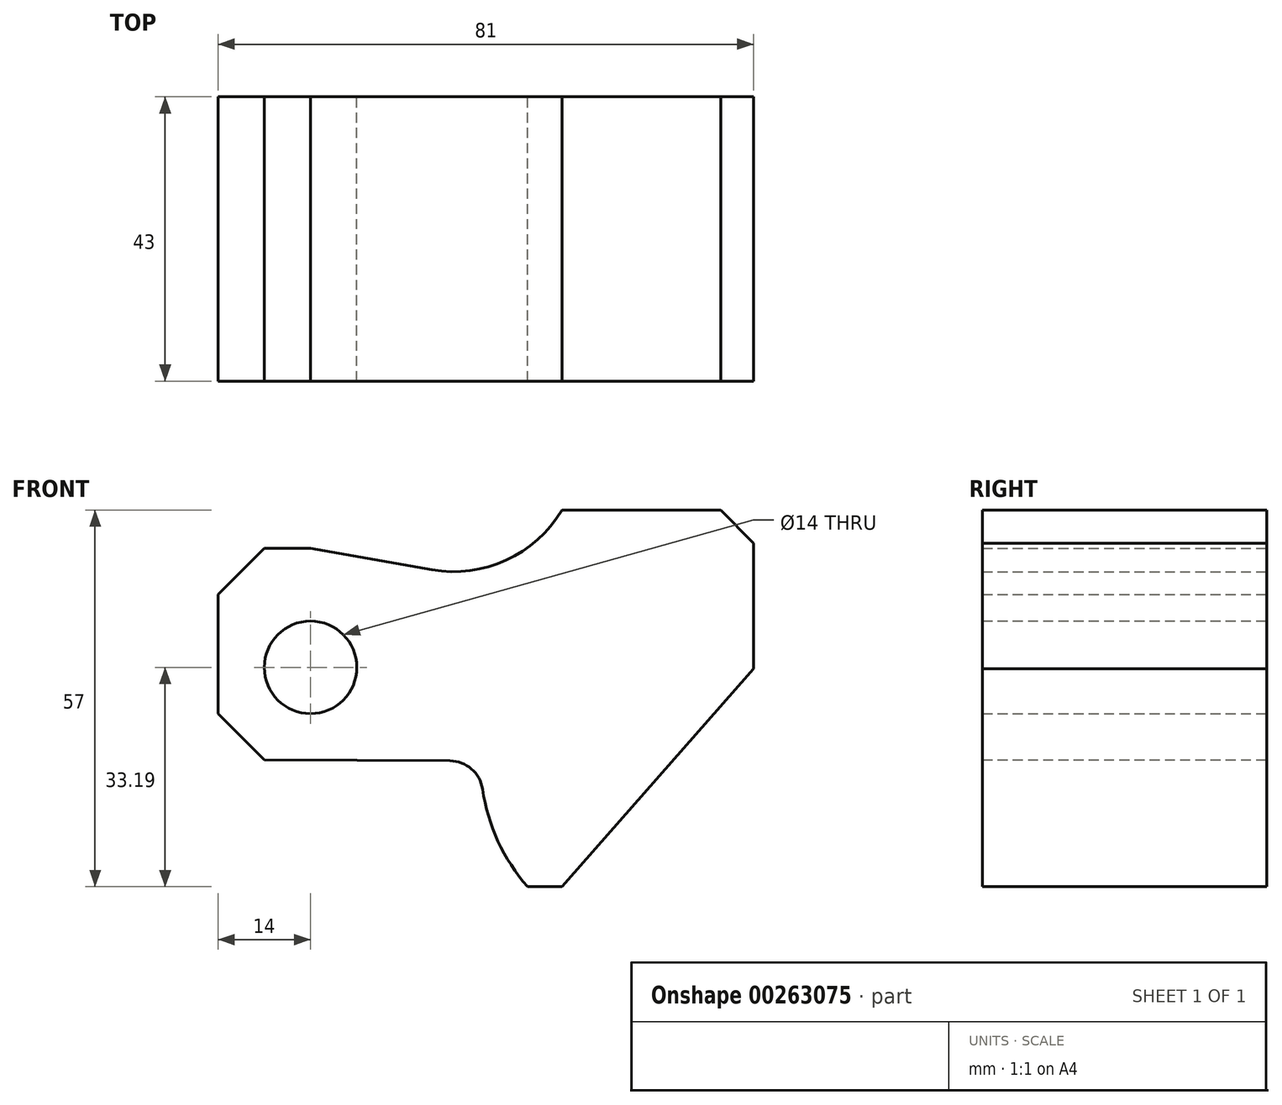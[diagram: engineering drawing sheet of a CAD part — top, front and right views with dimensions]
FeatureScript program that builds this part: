
annotation { "Feature Type Name" : "Feature", "Feature Type Description" : "" }
export const myFeature = defineFeature(function(context is Context, id is Id, definition is map)
    precondition{}
    {
        {
            var Q0;
            Q0=qCreatedBy(makeId("Front.planeOp"),FACE);
            var sketch = newSketch(context, id + "F0", { "sketchPlane" : qUnion([Q0])});
            skCircle(sketch, "E0", {"center": v(0, 0) * mm, "radius": 7 * mm});
            skLineSegment(sketch, "E1", {"start": v(-14, -7) * mm, "end": v(-14, 11) * mm});
            skLineSegment(sketch, "E2", {"start": v(-14, 11) * mm, "end": v(-7, 18) * mm});
            skLineSegment(sketch, "E3", {"start": v(-7, 18) * mm, "end": v(0, 18) * mm});
            skLineSegment(sketch, "E4", {"start": v(0, 18) * mm, "end": v(18.35, 14.77) * mm});
            skArc(sketch, "E5", {"start": v(18.35, 14.77) * mm, "mid": v(29.59, 16.22) * mm, "end": v(38, 23.8) * mm});
            skLineSegment(sketch, "E6", {"start": v(38, 23.8) * mm, "end": v(62, 23.8) * mm});
            skLineSegment(sketch, "E7", {"start": v(62, 23.8) * mm, "end": v(67, 18.8) * mm});
            skLineSegment(sketch, "E8", {"start": v(67, 18.8) * mm, "end": v(67, -0.2) * mm});
            skLineSegment(sketch, "E9", {"start": v(67, -0.2) * mm, "end": v(38, -33.2) * mm});
            skLineSegment(sketch, "E10", {"start": v(38, -33.2) * mm, "end": v(32.79, -33.2) * mm});
            skLineSegment(sketch, "E11", {"start": v(-7, -14) * mm, "end": v(-14, -7) * mm});
            skArc(sketch, "E12", {"start": v(26, -18.4) * mm, "mid": v(28.34, -26.29) * mm, "end": v(32.79, -33.2) * mm});
            skArc(sketch, "E13", {"start": v(26, -18.4) * mm, "mid": v(24.34, -15.36) * mm, "end": v(21.08, -14.14) * mm});
            skLineSegment(sketch, "E14", {"start": v(-7, -14) * mm, "end": v(21.08, -14.14) * mm});
            skSolve(sketch);
        }
        {
            var Q0;
            Q0 = qSketchRegion(id + "F0", true);
            extrude(context, id + "F1", {"entities" : qUnion([Q0]), "depth" : 43 * mm});
        }
    });
